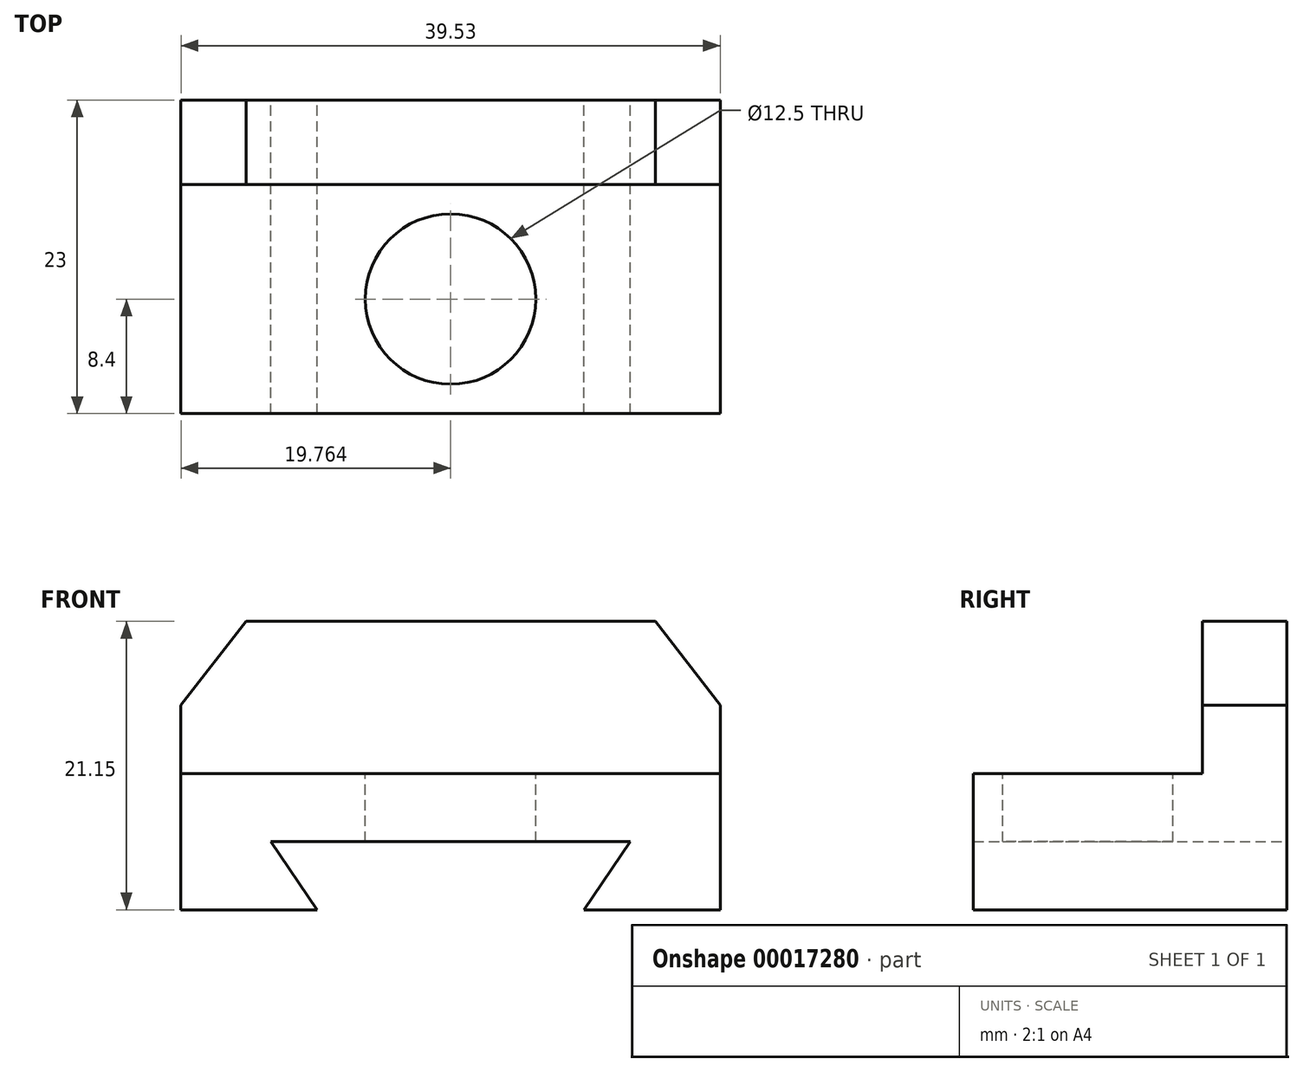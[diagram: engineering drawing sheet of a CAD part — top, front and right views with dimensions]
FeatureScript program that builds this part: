
annotation { "Feature Type Name" : "Feature", "Feature Type Description" : "" }
export const myFeature = defineFeature(function(context is Context, id is Id, definition is map)
    precondition{}
    {
        {
            var Q0;
            Q0=qCreatedBy(makeId("Front.planeOp"),FACE);
            var sketch = newSketch(context, id + "F0", { "sketchPlane" : qUnion([Q0])});
            skLineSegment(sketch, "E0", {"start": v(-25.99, 40.22) * mm, "end": v(4.01, 40.22) * mm});
            skLineSegment(sketch, "E1", {"start": v(-25.99, 40.22) * mm, "end": v(-30.75, 34.07) * mm});
            skLineSegment(sketch, "E2", {"start": v(4.01, 40.22) * mm, "end": v(8.78, 34.07) * mm});
            skLineSegment(sketch, "E3", {"start": v(-30.75, 34.07) * mm, "end": v(-30.75, 19.07) * mm});
            skLineSegment(sketch, "E4", {"start": v(8.78, 34.07) * mm, "end": v(8.78, 19.07) * mm});
            skLineSegment(sketch, "E5", {"start": v(-30.75, 19.07) * mm, "end": v(-20.75, 19.07) * mm});
            skLineSegment(sketch, "E6", {"start": v(8.78, 19.07) * mm, "end": v(-1.22, 19.07) * mm});
            skLineSegment(sketch, "E7", {"start": v(-20.75, 19.07) * mm, "end": v(-24.15, 24.07) * mm});
            skLineSegment(sketch, "E8", {"start": v(-24.15, 24.07) * mm, "end": v(2.18, 24.07) * mm});
            skLineSegment(sketch, "E9", {"start": v(-1.22, 19.07) * mm, "end": v(2.18, 24.07) * mm});
            skSolve(sketch);
        }
        {
            var Q0;
            Q0=makeQuery(id+"F0.imprint","IMPRINT",FACE,{"disambiguationData":[TD([[makeQuery(id+"F0.imprint","IMPRINT",EDGE,{"derivedFrom":sQuery(id+"F0.wireOp",EDGE,"E0")}),-1.0]])]});
            extrude(context, id + "F1", {"entities" : qUnion([Q0]), "depth" : 23 * mm});
        }
        {
            var Q0;
            Q0=makeQuery(id+"F1.opExtrude","CAP_FACE",FACE,{"disambiguationData":[OSD([sQuery(id+"F0.wireOp",EDGE,"E0"),sQuery(id+"F0.wireOp",EDGE,"E1"),sQuery(id+"F0.wireOp",EDGE,"E2"),sQuery(id+"F0.wireOp",EDGE,"E3"),sQuery(id+"F0.wireOp",EDGE,"E4"),sQuery(id+"F0.wireOp",EDGE,"E5"),sQuery(id+"F0.wireOp",EDGE,"E6"),sQuery(id+"F0.wireOp",EDGE,"E7"),sQuery(id+"F0.wireOp",EDGE,"E8"),sQuery(id+"F0.wireOp",EDGE,"E9")])],"isStart":false});
            var sketch = newSketch(context, id + "F2", { "sketchPlane" : qUnion([Q0])});
            skLineSegment(sketch, "E10", {"start": v(-30.75, 29.07) * mm, "end": v(8.78, 29.07) * mm});
            skLineSegment(sketch, "E11", {"start": v(-30.75, 29.07) * mm, "end": v(-30.75, 34.07) * mm});
            skLineSegment(sketch, "E12", {"start": v(-30.75, 34.07) * mm, "end": v(-25.99, 40.22) * mm});
            skLineSegment(sketch, "E13", {"start": v(-25.99, 40.22) * mm, "end": v(4.01, 40.22) * mm});
            skLineSegment(sketch, "E14", {"start": v(4.01, 40.22) * mm, "end": v(8.78, 34.07) * mm});
            skLineSegment(sketch, "E15", {"start": v(8.78, 29.07) * mm, "end": v(8.78, 34.07) * mm});
            skSolve(sketch);
        }
        {
            var Q0;
            Q0=makeQuery(id+"F2.imprint","IMPRINT",FACE,{"disambiguationData":[TD([[makeQuery(id+"F2.imprint","IMPRINT",EDGE,{"derivedFrom":sQuery(id+"F2.wireOp",EDGE,"E10")}),1.0]])]});
            extrude(context, id + "F3", {"entities" : qUnion([Q0]), "operationType" : NewBodyOperationType.REMOVE, "oppositeDirection" : true, "depth" : 16.8 * mm});
        }
        {
            var Q0;
            Q0=makeQuery(id+"F3.boolean.opBoolean","COPY",FACE,{"derivedFrom":makeQuery(id+"F3.opExtrude","SWEPT_FACE",FACE,{"disambiguationData":[OSD([sQuery(id+"F2.wireOp",EDGE,"E10")])]})});
            var sketch = newSketch(context, id + "F4", { "sketchPlane" : qUnion([Q0])});
            skCircle(sketch, "E16", {"center": v(-10.99, -14.6) * mm, "radius": 6.25 * mm});
            skSolve(sketch);
        }
        {
            var Q0;
            Q0=makeQuery(id+"F4.imprint","IMPRINT",FACE,{"disambiguationData":[TD([[makeQuery(id+"F4.imprint","IMPRINT",EDGE,{"derivedFrom":sQuery(id+"F4.wireOp",EDGE,"E16")}),1.0]])]});
            extrude(context, id + "F5", {"entities" : qUnion([Q0]), "operationType" : NewBodyOperationType.REMOVE, "oppositeDirection" : true, "depth" : 25 * mm});
        }
    });
